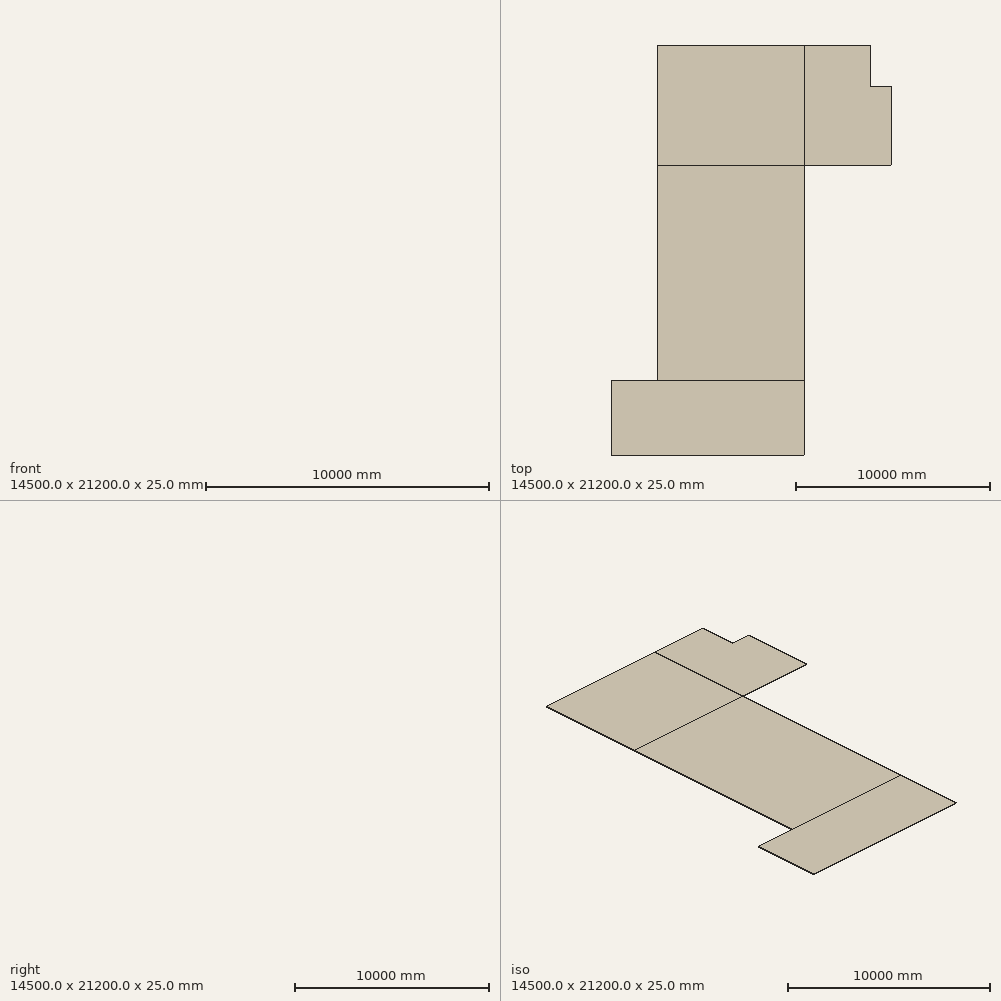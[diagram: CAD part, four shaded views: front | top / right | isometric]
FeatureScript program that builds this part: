
annotation { "Feature Type Name" : "Feature", "Feature Type Description" : "" }
export const myFeature = defineFeature(function(context is Context, id is Id, definition is map)
    precondition{}
    {
        {
            var Q0;
            Q0=qCreatedBy(makeId("Top.planeOp"),FACE);
            var sketch = newSketch(context, id + "F0", { "sketchPlane" : qUnion([Q0])});
            skLineSegment(sketch, "E0.bottom", {"start": v(0, 0) * mm, "end": v(7600, 0) * mm});
            skLineSegment(sketch, "E0.top", {"start": v(0, -6200) * mm, "end": v(7600, -6200) * mm});
            skLineSegment(sketch, "E0.left", {"start": v(0, 0) * mm, "end": v(0, -6200) * mm});
            skLineSegment(sketch, "E0.right", {"start": v(7600, 0) * mm, "end": v(7600, -6200) * mm});
            skSolve(sketch);
        }
        {
            var Q0;
            Q0 = qSketchRegion(id + "F0", true);
            extrude(context, id + "F1", {"entities" : qUnion([Q0]), "oppositeDirection" : true, "depth" : 25 * mm});
        }
        {
            var Q0;
            Q0=makeQuery(id+"F1.opExtrude","CAP_FACE",FACE,{"disambiguationData":[OSD([sQuery(id+"F0.wireOp",EDGE,"E0.bottom"),sQuery(id+"F0.wireOp",EDGE,"E0.top"),sQuery(id+"F0.wireOp",EDGE,"E0.left"),sQuery(id+"F0.wireOp",EDGE,"E0.right")])],"isStart":true});
            var sketch = newSketch(context, id + "F2", { "sketchPlane" : qUnion([Q0])});
            skLineSegment(sketch, "E1.bottom", {"start": v(0, -6200) * mm, "end": v(7600, -6200) * mm});
            skLineSegment(sketch, "E1.top", {"start": v(0, -17300) * mm, "end": v(7600, -17300) * mm});
            skLineSegment(sketch, "E1.left", {"start": v(0, -6200) * mm, "end": v(0, -17300) * mm});
            skLineSegment(sketch, "E1.right", {"start": v(7600, -6200) * mm, "end": v(7600, -17300) * mm});
            skSolve(sketch);
        }
        {
            var Q0;
            Q0 = qSketchRegion(id + "F2", true);
            extrude(context, id + "F3", {"entities" : qUnion([Q0]), "oppositeDirection" : true, "depth" : 25 * mm});
        }
        {
            var Q0;
            Q0=makeQuery(id+"F3.boolean.opBoolean","MERGE",FACE,{"derivedFrom":[makeQuery(id+"F1.opExtrude","CAP_FACE",FACE,{"disambiguationData":[OSD([sQuery(id+"F0.wireOp",EDGE,"E0.bottom"),sQuery(id+"F0.wireOp",EDGE,"E0.top"),sQuery(id+"F0.wireOp",EDGE,"E0.left"),sQuery(id+"F0.wireOp",EDGE,"E0.right")])],"isStart":true}),makeQuery(id+"F3.opExtrude","CAP_FACE",FACE,{"disambiguationData":[OSD([sQuery(id+"F2.wireOp",EDGE,"E1.bottom"),sQuery(id+"F2.wireOp",EDGE,"E1.top"),sQuery(id+"F2.wireOp",EDGE,"E1.left"),sQuery(id+"F2.wireOp",EDGE,"E1.right")])],"isStart":true})]});
            var sketch = newSketch(context, id + "F4", { "sketchPlane" : qUnion([Q0])});
            skLineSegment(sketch, "E2.bottom", {"start": v(7600, -17300) * mm, "end": v(-2400, -17300) * mm});
            skLineSegment(sketch, "E2.top", {"start": v(7600, -21200) * mm, "end": v(-2400, -21200) * mm});
            skLineSegment(sketch, "E2.left", {"start": v(7600, -17300) * mm, "end": v(7600, -21200) * mm});
            skLineSegment(sketch, "E2.right", {"start": v(-2400, -17300) * mm, "end": v(-2400, -21200) * mm});
            skSolve(sketch);
        }
        {
            var Q0;
            Q0 = qSketchRegion(id + "F4", true);
            extrude(context, id + "F5", {"entities" : qUnion([Q0]), "oppositeDirection" : true, "depth" : 25 * mm});
        }
        {
            var Q0;
            Q0=makeQuery(id+"F5.boolean.opBoolean","MERGE",FACE,{"derivedFrom":[makeQuery(id+"F3.boolean.opBoolean","MERGE",FACE,{"derivedFrom":[makeQuery(id+"F1.opExtrude","CAP_FACE",FACE,{"disambiguationData":[OSD([sQuery(id+"F0.wireOp",EDGE,"E0.bottom"),sQuery(id+"F0.wireOp",EDGE,"E0.top"),sQuery(id+"F0.wireOp",EDGE,"E0.left"),sQuery(id+"F0.wireOp",EDGE,"E0.right")])],"isStart":true}),makeQuery(id+"F3.opExtrude","CAP_FACE",FACE,{"disambiguationData":[OSD([sQuery(id+"F2.wireOp",EDGE,"E1.bottom"),sQuery(id+"F2.wireOp",EDGE,"E1.top"),sQuery(id+"F2.wireOp",EDGE,"E1.left"),sQuery(id+"F2.wireOp",EDGE,"E1.right")])],"isStart":true})]}),makeQuery(id+"F5.opExtrude","CAP_FACE",FACE,{"disambiguationData":[OSD([sQuery(id+"F4.wireOp",EDGE,"E2.bottom"),sQuery(id+"F4.wireOp",EDGE,"E2.top"),sQuery(id+"F4.wireOp",EDGE,"E2.left"),sQuery(id+"F4.wireOp",EDGE,"E2.right")])],"isStart":true})]});
            var sketch = newSketch(context, id + "F6", { "sketchPlane" : qUnion([Q0])});
            skLineSegment(sketch, "E3.bottom", {"start": v(7600, 0) * mm, "end": v(11000, 0) * mm});
            skLineSegment(sketch, "E3.top", {"start": v(7600, -6200) * mm, "end": v(11000, -6200) * mm});
            skLineSegment(sketch, "E3.left", {"start": v(7600, 0) * mm, "end": v(7600, -6200) * mm});
            skLineSegment(sketch, "E3.right", {"start": v(11000, 0) * mm, "end": v(11000, -6200) * mm});
            skSolve(sketch);
        }
        {
            var Q0;
            Q0 = qSketchRegion(id + "F6", true);
            extrude(context, id + "F7", {"entities" : qUnion([Q0]), "oppositeDirection" : true, "depth" : 25 * mm});
        }
        {
            var Q0;
            Q0=makeQuery(id+"F7.boolean.opBoolean","MERGE",FACE,{"derivedFrom":[makeQuery(id+"F5.boolean.opBoolean","MERGE",FACE,{"derivedFrom":[makeQuery(id+"F3.boolean.opBoolean","MERGE",FACE,{"derivedFrom":[makeQuery(id+"F1.opExtrude","CAP_FACE",FACE,{"disambiguationData":[OSD([sQuery(id+"F0.wireOp",EDGE,"E0.bottom"),sQuery(id+"F0.wireOp",EDGE,"E0.top"),sQuery(id+"F0.wireOp",EDGE,"E0.left"),sQuery(id+"F0.wireOp",EDGE,"E0.right")])],"isStart":true}),makeQuery(id+"F3.opExtrude","CAP_FACE",FACE,{"disambiguationData":[OSD([sQuery(id+"F2.wireOp",EDGE,"E1.bottom"),sQuery(id+"F2.wireOp",EDGE,"E1.top"),sQuery(id+"F2.wireOp",EDGE,"E1.left"),sQuery(id+"F2.wireOp",EDGE,"E1.right")])],"isStart":true})]}),makeQuery(id+"F5.opExtrude","CAP_FACE",FACE,{"disambiguationData":[OSD([sQuery(id+"F4.wireOp",EDGE,"E2.bottom"),sQuery(id+"F4.wireOp",EDGE,"E2.top"),sQuery(id+"F4.wireOp",EDGE,"E2.left"),sQuery(id+"F4.wireOp",EDGE,"E2.right")])],"isStart":true})]}),makeQuery(id+"F7.opExtrude","CAP_FACE",FACE,{"disambiguationData":[OSD([sQuery(id+"F6.wireOp",EDGE,"E3.bottom"),sQuery(id+"F6.wireOp",EDGE,"E3.top"),sQuery(id+"F6.wireOp",EDGE,"E3.left"),sQuery(id+"F6.wireOp",EDGE,"E3.right")])],"isStart":true})]});
            var sketch = newSketch(context, id + "F8", { "sketchPlane" : qUnion([Q0])});
            skLineSegment(sketch, "E4.bottom", {"start": v(11000, -2100) * mm, "end": v(12100, -2100) * mm});
            skLineSegment(sketch, "E4.top", {"start": v(11000, -6200) * mm, "end": v(12100, -6200) * mm});
            skLineSegment(sketch, "E4.left", {"start": v(11000, -2100) * mm, "end": v(11000, -6200) * mm});
            skLineSegment(sketch, "E4.right", {"start": v(12100, -2100) * mm, "end": v(12100, -6200) * mm});
            skSolve(sketch);
        }
        {
            var Q0;
            Q0 = qSketchRegion(id + "F8", true);
            extrude(context, id + "F9", {"entities" : qUnion([Q0]), "operationType" : NewBodyOperationType.ADD, "oppositeDirection" : true, "depth" : 25 * mm});
        }
    });
